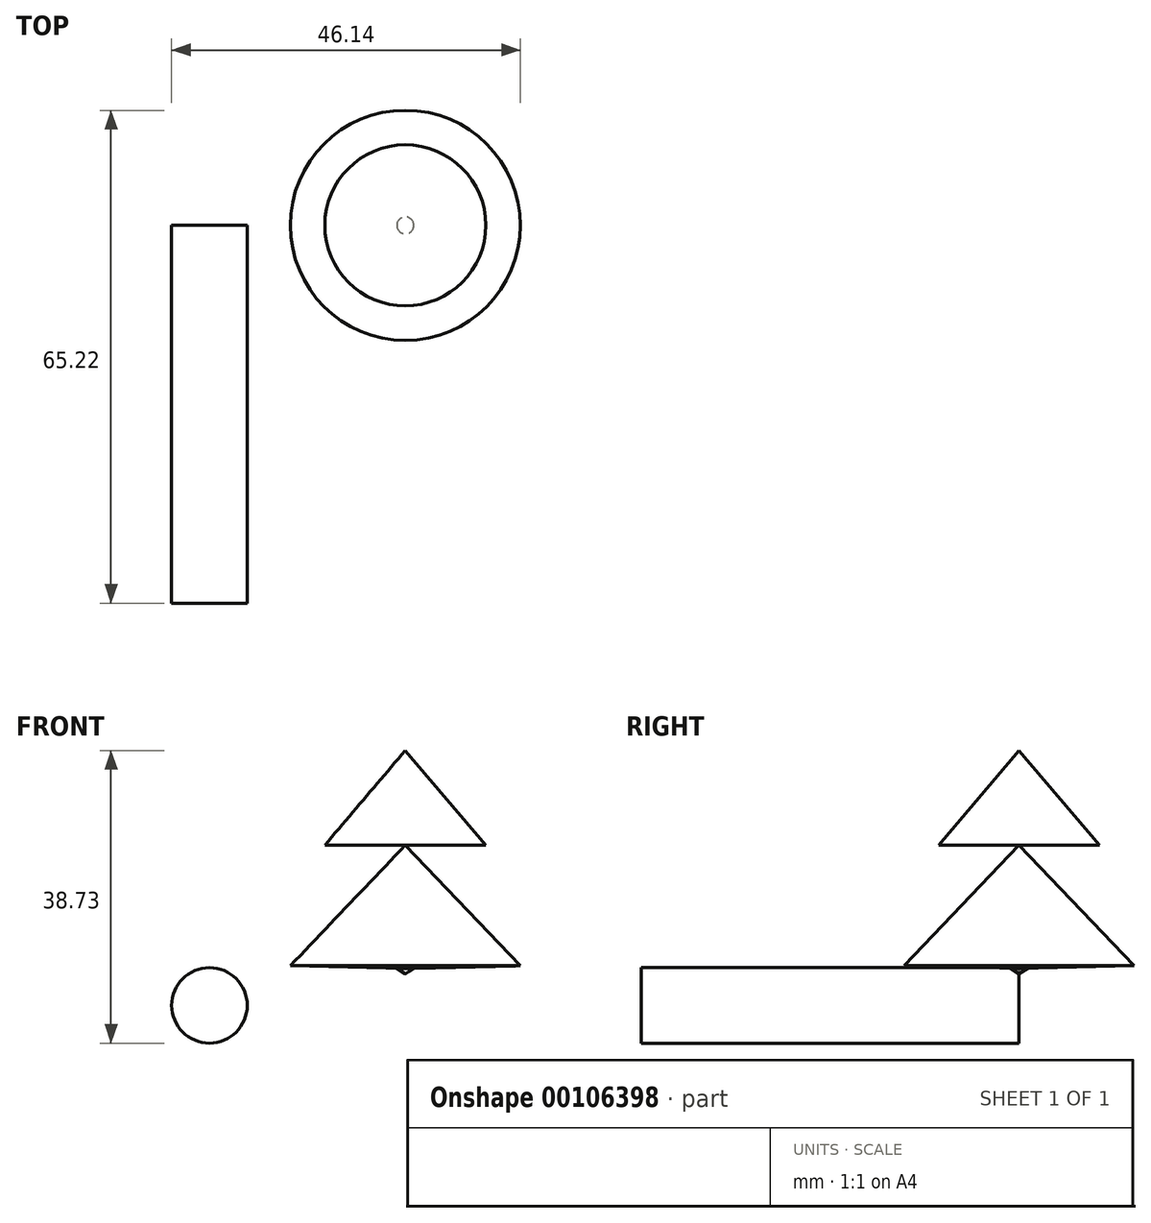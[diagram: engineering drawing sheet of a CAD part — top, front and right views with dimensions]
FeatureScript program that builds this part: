
annotation { "Feature Type Name" : "Feature", "Feature Type Description" : "" }
export const myFeature = defineFeature(function(context is Context, id is Id, definition is map)
    precondition{}
    {
        {
            var Q0;
            Q0=qCreatedBy(makeId("Front.planeOp"),FACE);
            var sketch = newSketch(context, id + "F0", { "sketchPlane" : qUnion([Q0])});
            skCircle(sketch, "E0", {"center": v(-25.92, 24.87) * mm, "radius": 5 * mm});
            skSolve(sketch);
        }
        {
            var Q0;
            Q0=makeQuery(id+"F0.imprint","IMPRINT",FACE,{"disambiguationData":[TD([[makeQuery(id+"F0.imprint","IMPRINT",EDGE,{"derivedFrom":sQuery(id+"F0.wireOp",EDGE,"E0")}),1.0]])]});
            extrude(context, id + "F1", {"entities" : qUnion([Q0]), "depth" : 50 * mm});
        }
        {
            var Q0;
            Q0=qCreatedBy(makeId("Front.planeOp"),FACE);
            var sketch = newSketch(context, id + "F2", { "sketchPlane" : qUnion([Q0])});
            skLineSegment(sketch, "E1", {"start": v(0, 68.1) * mm, "end": v(0, -60.7) * mm});
            skLineSegment(sketch, "E2", {"start": v(0, 58.6) * mm, "end": v(-10.66, 46.07) * mm});
            skLineSegment(sketch, "E3", {"start": v(-10.66, 46.07) * mm, "end": v(0, 46.07) * mm});
            skLineSegment(sketch, "E4", {"start": v(0, 46.07) * mm, "end": v(-15.22, 30.1) * mm});
            skLineSegment(sketch, "E5", {"start": v(-15.22, 30.1) * mm, "end": v(1.12, 29.73) * mm});
            skLineSegment(sketch, "E6", {"start": v(1.12, 29.73) * mm, "end": v(-23.96, 14.53) * mm});
            skLineSegment(sketch, "E7", {"start": v(-23.96, 14.53) * mm, "end": v(-6.86, 14.53) * mm});
            skLineSegment(sketch, "E8", {"start": v(-6.86, 14.53) * mm, "end": v(-6.86, 0) * mm});
            skLineSegment(sketch, "E9", {"start": v(-6.86, 0) * mm, "end": v(0, 0) * mm});
            skSolve(sketch);
        }
        {
            var Q0;
            {var subQ0=sQuery(id+"F2.wireOp",EDGE,"E2");Q0=makeQuery(id+"F2.imprint","IMPRINT",FACE,{"disambiguationData":[TD([[makeQuery(id+"F2.imprint","IMPRINT",EDGE,{"derivedFrom":subQ0}),1.0]])]});}
            var Q1;
            {var subQ0=sQuery(id+"F2.wireOp",EDGE,"E4");Q1=makeQuery(id+"F2.imprint","IMPRINT",FACE,{"disambiguationData":[TD([[makeQuery(id+"F2.imprint","IMPRINT",EDGE,{"derivedFrom":subQ0}),1.0]])]});}
            var Q2;
            {var subQ0=sQuery(id+"F2.wireOp",EDGE,"E5");var subQ1=sQuery(id+"F2.wireOp",EDGE,"E1");var subQ2=makeQuery(id+"F2.imprint","INTERSECT",VERTEX,{"derivedFrom":[subQ1,subQ0]});Q2=makeQuery(id+"F2.imprint","IMPRINT",FACE,{"disambiguationData":[TD([[makeQuery(id+"F2.imprint","IMPRINT",EDGE,{"disambiguationData":[TD([[subQ2,-1.0]])],"derivedFrom":subQ1}),1.0]])]});}
            var Q3;
            Q3=sQuery(id+"F2.wireOp",EDGE,"E1");
            revolve(context, id + "F3", {"entities" : qUnion([Q0, Q1, Q2]), "axis" : qUnion([Q3]), "revolveType" : RevolveType.FULL});
        }
    });
